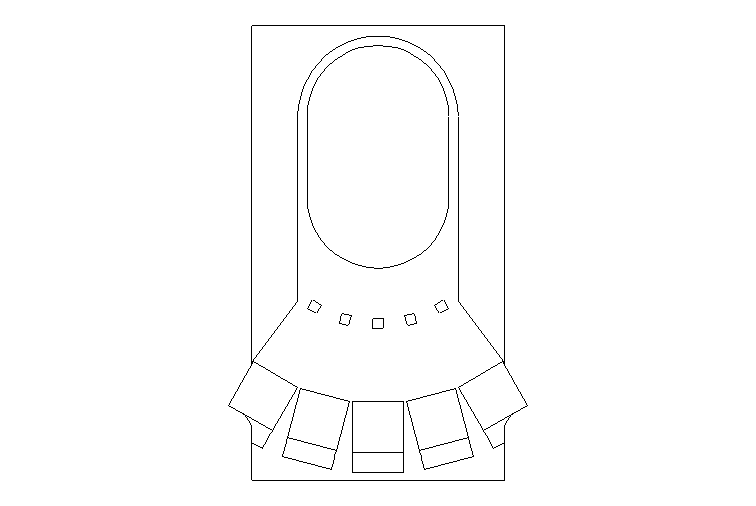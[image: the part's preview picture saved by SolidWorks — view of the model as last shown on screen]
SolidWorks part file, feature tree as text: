
SOLIDWORKS PART (.sldprt)
format: sldprt  version: not decoded by parser v0  size: 301,056 bytes
history: native  units: mm
features: sketch x10, extrude x10, plane x3, fillet x1 + 2 further entries
feature tree (26):
  plane  "Plane1"
  plane  "Plane2"
  plane  "Plane3"
  "Origin"
  sketch  "Sketch1"  dims[D1=25.0mm D2=45.0mm D3=12.5mm D4=25.0mm]
  extrude  "Base-Extrude"  Depth=3mm
  sketch  "Sketch2"  dims[c1.D1=7.0mm c1.D2=7.0mm c1.D3=4.0mm c1.D4=15.0mm c1.D5=26.0mm c2.D2=7.0mm c2.D4=7.0mm c3.D2=7.0mm c3.D1=8.0mm c3.D6=22.0mm c4.D6=37.5deg c5.D6=22.0mm c6.D6=37.5deg c6.D3=~10.313593mm c6.D4=~3.426796mm c7.D3=13.0mm c7.D4=~2.086101mm c8.D3=13.0mm c8.D4=8.0mm]
  extrude  "Boss-Extrude1"  Depth=17mm
  sketch  "Sketch3"  dims[c1.D1=1.0mm c1.D2=1.0mm c1.D3=13.0mm c1.D4=13.0mm c2.D4=7.5deg c2.D5=~18.248288mm c3.D5=7.5deg c3.D6=5.0mm c3.D7=5.0mm c3.D8=7.2mm c3.D9=2.5mm c3.D10=8.0mm c3.D11=20.2mm]
  extrude  "Boss-Extrude2"  Depth=1mm
  sketch  "Sketch5"  dims[D2=~33.290317mm D1=0.0mm]
  extrude  "Boss-Extrude3"  Depth=16mm
  sketch  "Sketch6"  dims[D1=0.0mm]
  extrude  "Boss-Extrude4"  Depth=16mm
  sketch  "Sketch7"  dims[D1=0.0mm]
  extrude  "Boss-Extrude5"  Depth=16mm
  sketch  "Sketch8"  dims[D1=0.0mm]
  extrude  "Boss-Extrude6"  Depth=16mm
  sketch  "Sketch9"  dims[D1=0.0mm]
  extrude  "Boss-Extrude7"  Depth=16mm
  sketch  "Sketch10"  dims[D1=0.0mm]
  extrude  "Boss-Extrude8"  Depth=3mm
  sketch  "Sketch11"  dims[D1=0.0mm]
  extrude  "Boss-Extrude9"  Depth=3mm
  fillet  "Fillet1"  Radius=2mm
  "Annotations"  RD1=0.913899mm RD3=7mm RD4=20mm RD5=1mm RD2=17.54537mm
decode coverage: 21 of 21 modeling features carry decoded parameters; 2 rows unclassified (native names shown)
note: ~ marks probable driven/reference dimensions
note: suppression state not decoded; provenance and decode notes live in map.json
